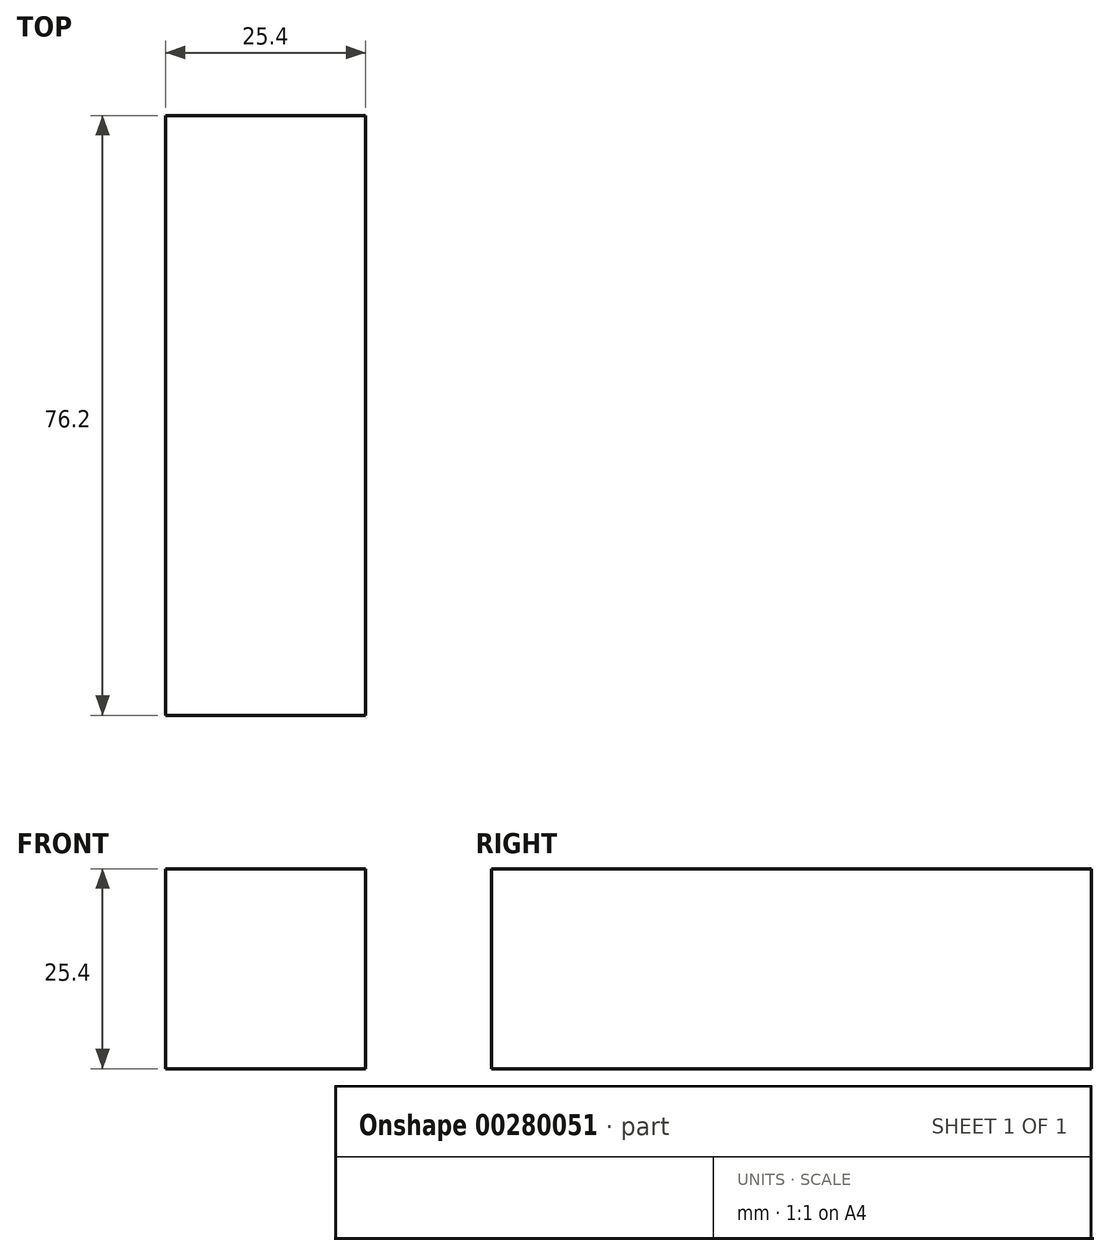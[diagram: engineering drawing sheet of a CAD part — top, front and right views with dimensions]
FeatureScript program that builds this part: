
annotation { "Feature Type Name" : "Feature", "Feature Type Description" : "" }
export const myFeature = defineFeature(function(context is Context, id is Id, definition is map)
    precondition{}
    {
        {
            var Q0;
            Q0=qCreatedBy(makeId("Front.planeOp"),FACE);
            var sketch = newSketch(context, id + "F0", { "sketchPlane" : qUnion([Q0])});
            skLineSegment(sketch, "E0.bottom", {"start": v(0, 0) * mm, "end": v(-25.4, 0) * mm});
            skLineSegment(sketch, "E0.top", {"start": v(0, 25.4) * mm, "end": v(-25.4, 25.4) * mm});
            skLineSegment(sketch, "E0.left", {"start": v(0, 0) * mm, "end": v(0, 25.4) * mm});
            skLineSegment(sketch, "E0.right", {"start": v(-25.4, 0) * mm, "end": v(-25.4, 25.4) * mm});
            skSolve(sketch);
        }
        {
            var Q0;
            Q0=makeQuery(id+"F0.imprint","IMPRINT",FACE,{"disambiguationData":[TD([[makeQuery(id+"F0.imprint","IMPRINT",EDGE,{"derivedFrom":sQuery(id+"F0.wireOp",EDGE,"E0.bottom")}),-1.0]])]});
            extrude(context, id + "F1", {"entities" : qUnion([Q0]), "depth" : 76.2 * mm});
        }
    });
